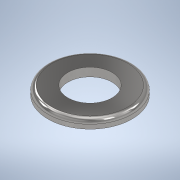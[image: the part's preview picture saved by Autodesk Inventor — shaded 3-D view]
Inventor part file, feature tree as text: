
AUTODESK INVENTOR PART (.ipt)
format: ipt  version: 2020 (Build 240168000, 168)  size: 129,536 bytes
history: native  units: in
note: dims shown in document units (in); Inventor stores cm internally (conversion verified against a paired STEP export)
features: extrude x1, fillet x1, sketch x1
ambient origin geometry x8: Origin, YZ Plane, XZ Plane, XY Plane, X Axis, Y Axis, Z Axis, Center Point
bodies: Solid1 (feature_tree)
feature tree (3):
  extrude  "Extrusion1"  Depth=0.0625in
  fillet  "Fillet2"  Radius=0.125in
  sketch  "Sketch1"  dims[d0=1.25in d1=0.6562in d2=0.125in d3=0.0in d5=0.0625in]
